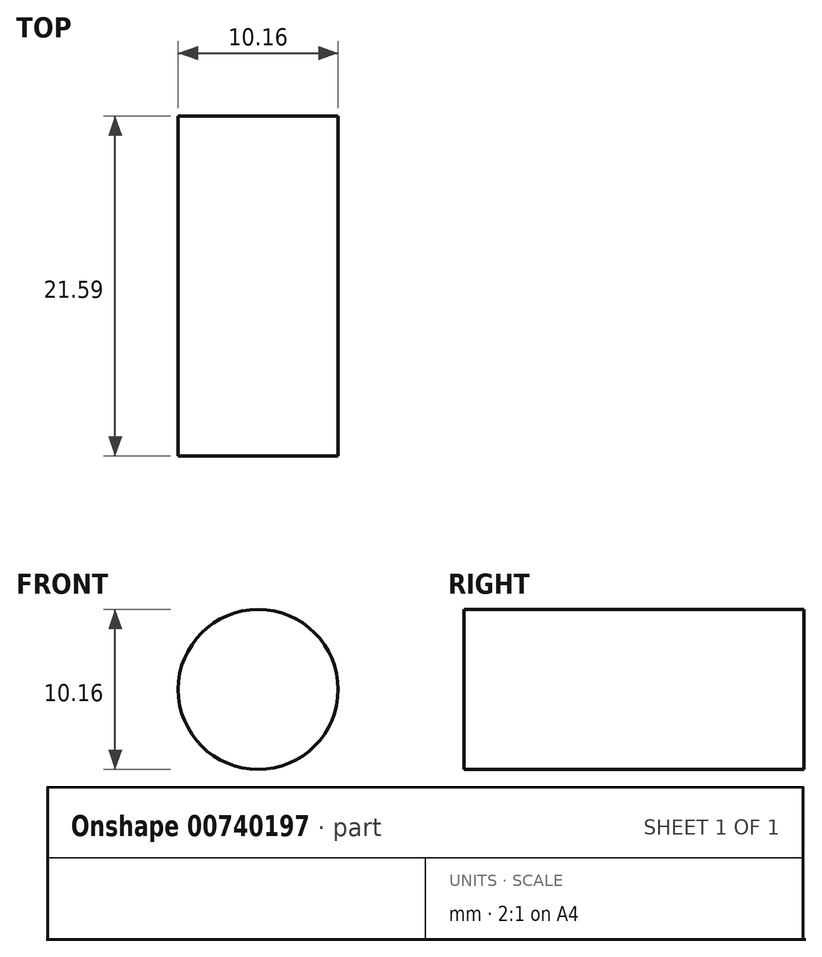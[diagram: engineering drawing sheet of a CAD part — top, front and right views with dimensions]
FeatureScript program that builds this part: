
annotation { "Feature Type Name" : "Feature", "Feature Type Description" : "" }
export const myFeature = defineFeature(function(context is Context, id is Id, definition is map)
    precondition{}
    {
        {
            var Q0;
            Q0=qCreatedBy(makeId("Front.planeOp"),FACE);
            var sketch = newSketch(context, id + "F0", { "sketchPlane" : qUnion([Q0])});
            skCircle(sketch, "E0", {"center": v(0, 0) * mm, "radius": 5.08 * mm});
            skSolve(sketch);
        }
        {
            var Q0;
            Q0 = qSketchRegion(id + "F0", true);
            extrude(context, id + "F1", {"entities" : qUnion([Q0]), "depth" : 21.59 * mm, "offsetDistance" : 25.4 * mm});
        }
    });
